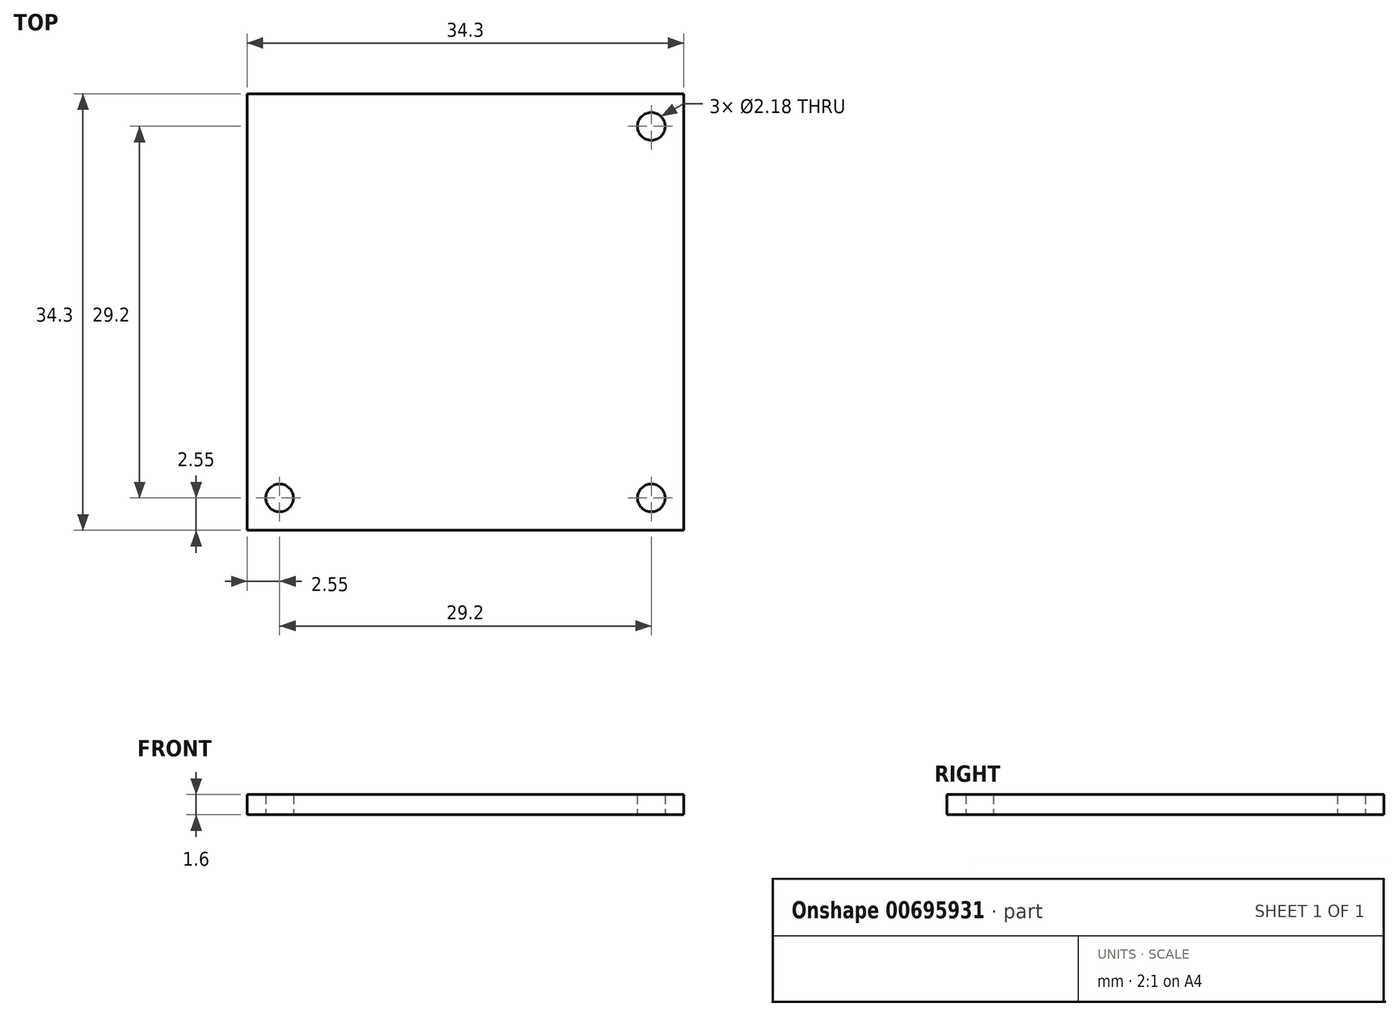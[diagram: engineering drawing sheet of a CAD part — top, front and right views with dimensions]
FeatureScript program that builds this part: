
annotation { "Feature Type Name" : "Feature", "Feature Type Description" : "" }
export const myFeature = defineFeature(function(context is Context, id is Id, definition is map)
    precondition{}
    {
        {
            var Q0;
            Q0=qCreatedBy(makeId("Top.planeOp"),FACE);
            var sketch = newSketch(context, id + "F0", { "sketchPlane" : qUnion([Q0])});
            skLineSegment(sketch, "E0.bottom", {"start": v(17.15, -17.15) * mm, "end": v(-17.15, -17.15) * mm});
            skLineSegment(sketch, "E0.top", {"start": v(17.15, 17.15) * mm, "end": v(-17.15, 17.15) * mm});
            skLineSegment(sketch, "E0.left", {"start": v(17.15, -17.15) * mm, "end": v(17.15, 17.15) * mm});
            skLineSegment(sketch, "E0.right", {"start": v(-17.15, -17.15) * mm, "end": v(-17.15, 17.15) * mm});
            skPoint(sketch, "E0.middle", {"position": v(0, 0) * mm});
            skLineSegment(sketch, "E1.bottom", {"start": v(14.6, -14.6) * mm, "end": v(-14.6, -14.6) * mm, "construction": true});
            skLineSegment(sketch, "E1.top", {"start": v(14.6, 14.6) * mm, "end": v(-14.6, 14.6) * mm, "construction": true});
            skLineSegment(sketch, "E1.left", {"start": v(14.6, -14.6) * mm, "end": v(14.6, 14.6) * mm, "construction": true});
            skLineSegment(sketch, "E1.right", {"start": v(-14.6, -14.6) * mm, "end": v(-14.6, 14.6) * mm, "construction": true});
            skCircle(sketch, "E2", {"center": v(14.6, 14.6) * mm, "radius": 1.09 * mm});
            skCircle(sketch, "E3", {"center": v(14.6, -14.6) * mm, "radius": 1.09 * mm});
            skCircle(sketch, "E4", {"center": v(-14.6, -14.6) * mm, "radius": 1.09 * mm});
            skSolve(sketch);
        }
        {
            var Q0;
            Q0 = qSketchRegion(id + "F0", true);
            extrude(context, id + "F1", {"entities" : qUnion([Q0]), "depth" : 1.6 * mm, "offsetDistance" : 25 * mm});
        }
    });
